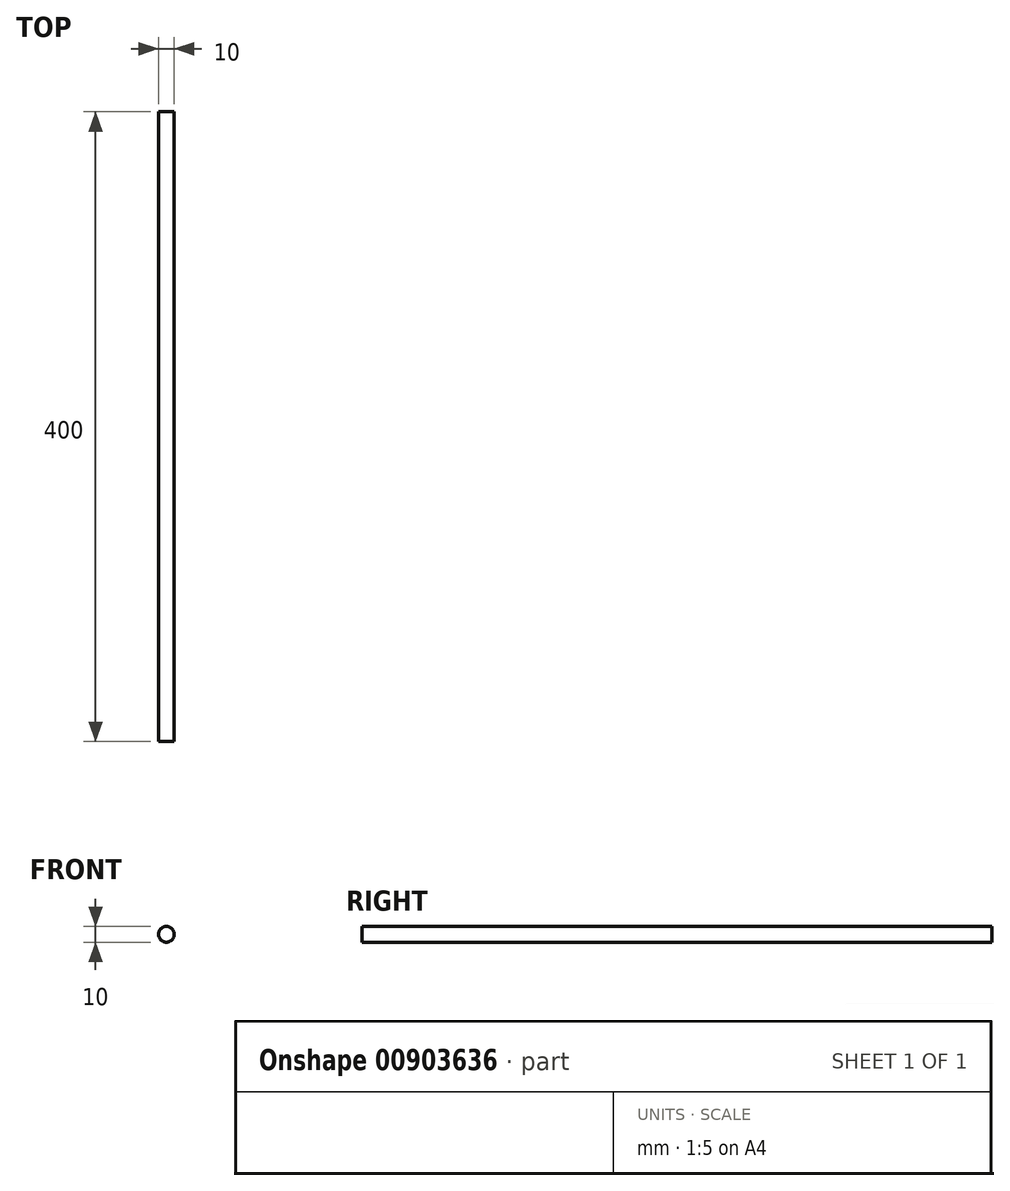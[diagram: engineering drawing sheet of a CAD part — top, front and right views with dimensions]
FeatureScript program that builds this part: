
annotation { "Feature Type Name" : "Feature", "Feature Type Description" : "" }
export const myFeature = defineFeature(function(context is Context, id is Id, definition is map)
    precondition{}
    {
        {
            var Q0;
            Q0=qCreatedBy(makeId("Front.planeOp"),FACE);
            var sketch = newSketch(context, id + "F0", { "sketchPlane" : qUnion([Q0])});
            skCircle(sketch, "E0", {"center": v(0, 0) * mm, "radius": 5 * mm});
            skSolve(sketch);
        }
        {
            var Q0;
            Q0=qSketchRegion(id+"F0",true);
            extrude(context, id + "F1", {"entities" : qUnion([Q0]), "depth" : 400 * mm});
        }
    });
